# Revit family: Shower-Bath_Shower-STERLING-Accord-71140113_1
name_source: partatom
category: Plumbing Fixtures
revit_build: Autodesk Revit 2017 (Build: 20160225_1515(x64)
units: mm (PartAtom-declared; Revit-internal decimal feet)

## family parameters
Cut with Voids When Loaded = No
Host = Face
OmniClass Number = 23.31.15.11
OmniClass Title = Bath Shower Units
Part Type = Normal
Room Calculation Point = No
Round Connector Dimension = Use Diameter
Shared = No

## types (4) — shared parameters
ADA Compliant = No
Assembly Code = D2010500
CW Connection = No
Cold Water Inlet = Cold Water Inlet
Date Modified = 06/29/2020
Default Elevation = 0"
Description = 60 inch bath/shower with Aging in Place grab bars
Drain Included = No
HW Connection = No
Height = 73 1/4"
Hot Water Inlet = Hot Water Inlet
Length = 60"
Manufacturer = STERLING Co.
Master Format 2014 = 22 41 19
Master Format 2014 Name = Residential Bathtubs
Material = Vikrell
Product Documentation Link = https://resources.kohler.com
Product Name = Accord
Product Page URL = http://www.sterlingplumbing.com
URL = https://www.sterlingplumbing.com
Vent Connection = No
Waste Connection = Yes
Waste Water Outlet = Waste Water Outlet
WaterSense Certified = No
Width = 31 1/4"

## per-type parameters (varying)
| type | Finish | Grab Bar Material | Model | Type |
| Matte Silver Grab Bar, 0-White | Sterling-Vikrell-0-White | Sterling-Metal-V-Matte_Silver | 71140113-V-0 | 3 |
| Matte Silver Grab Bar, 96-Biscuit | Sterling-Vikrell-96-Biscuit | Sterling-Metal-V-Matte_Silver | 71140113-V-96 | 4 |
| Nickel Grab Bar, 0-White | Sterling-Vikrell-0-White | Sterling-Metal-N-Nickel | 71140113-N-0 | 1 |
| Nickel Grab Bar, 96-Biscuit | Sterling-Vikrell-96-Biscuit | Sterling-Metal-N-Nickel | 71140113-N-96 | 2 |

## geometry (parser evidence)
native form markers: Sweep x2
no freeform markers — native parametric forms only
